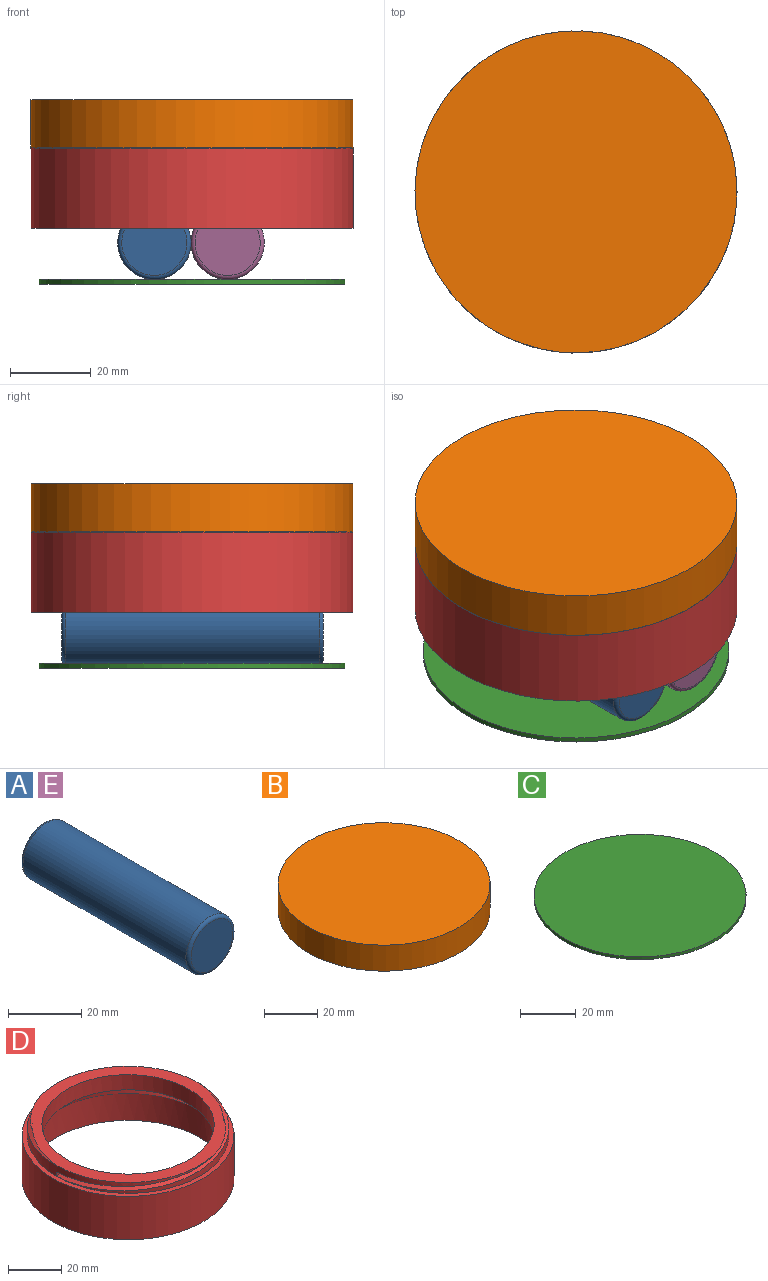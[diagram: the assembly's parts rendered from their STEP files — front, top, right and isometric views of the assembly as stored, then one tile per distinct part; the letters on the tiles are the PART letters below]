
ASSEMBLY  parts=5 mates=3
PART A: 5 faces, bbox 19.7x65x19.7 mm
  f0: cylinder r=9.1mm len=63mm, axis (0,1,0), area 3602.2mm2, adj f3,f4
  f1: plane 16.2x16.2mm, normal (0,-1,0), area 206.1mm2, adj f4
  f2: plane 16.2x16.2mm, normal (0,1,0), area 206.1mm2, adj f3
  f3: torus R=8.1mm, axis (0,-1,0), area 86.2mm2, adj f0,f2
  f4: torus R=8.1mm, axis (0,-1,0), area 86.2mm2, adj f0,f1
PART B: 14 faces, bbox 80.5x80.5x12.5 mm
  f0: cylinder r=38mm len=76mm, axis (0,0,-1), area 406mm2, adj f4,f6,f8,f10,f12
  f1: cylinder r=38mm len=76mm, axis (0,0,-1), area 406mm2, adj f4,f6,f9,f11,f13
  f2: cylinder r=40mm len=80mm, axis (0,0,-1), area 3015.9mm2, adj f3,f4
  f3: plane 80x80mm, normal (0,0,1), area 5026.5mm2, adj f2
  f4: plane 80x80mm, normal (0,0,-1), area 490.1mm2, adj f0,f1,f2
  f5: cylinder r=36mm len=72mm, axis (0,0,1), area 1131mm2, adj f6,f7
  f6: plane 76.52x76.52mm, normal (0,0,-1), area 383.5mm2, adj f0,f1,f5,f9,f10,f12,f13
  f7: plane 72x72mm, normal (0,0,-1), area 4071.5mm2, adj f5
  f8: plane 2x1.73mm, normal (0,-1,0), area 1.7mm2, adj f0,f9,f10
  f9: bspline ~76x38mm, area 210.6mm2, adj f1,f6,f8,f10
  f10: bspline ~76x38mm, area 163.6mm2, adj f0,f6,f8,f9
  f11: plane 2x1.73mm, normal (0,1,0), area 1.7mm2, adj f1,f12,f13
  f12: bspline ~76x38mm, area 210.6mm2, adj f0,f6,f11,f13
  f13: bspline ~76x38mm, area 163.6mm2, adj f1,f6,f11,f12
PART C: 3 faces, bbox 76x76x1.2 mm
  f0: cylinder r=38mm len=76mm, axis (0,0,-1), area 286.5mm2, adj f1,f2
  f1: plane 76x76mm, normal (0,0,1), area 4536.5mm2, adj f0
  f2: plane 76x76mm, normal (0,0,-1), area 4536.5mm2, adj f0
PART D: 15 faces, bbox 80.2x80.2x27.2 mm
  f0: cylinder r=32.5mm len=65mm, axis (0,0,1), area 1429.4mm2, adj f6,f14
  f1: cylinder r=38mm len=76mm, axis (0,0,1), area 406mm2, adj f5,f6,f7,f8,f12
  f2: cylinder r=38mm len=76mm, axis (0,0,1), area 406mm2, adj f5,f6,f9,f10,f11
  f3: cylinder r=40mm len=80mm, axis (0,0,-1), area 5026.5mm2, adj f4,f5
  f4: plane 80x80mm, normal (0,0,-1), area 490.1mm2, adj f3,f13
  f5: plane 80x80mm, normal (0,0,1), area 490.1mm2, adj f1,f2,f3
  f6: plane 76.17x76.17mm, normal (0,0,1), area 1136.7mm2, adj f0,f1,f2,f8,f9,f11,f12
  f7: plane 2x1.73mm, normal (0,1,0), area 1.7mm2, adj f1,f8,f9
  f8: bspline ~76x38mm, area 163.3mm2, adj f1,f6,f7,f9
  f9: bspline ~76x38mm, area 210.7mm2, adj f2,f6,f7,f8
  f10: plane 2x1.73mm, normal (0,-1,0), area 1.7mm2, adj f2,f11,f12
  f11: bspline ~76x38mm, area 163.3mm2, adj f2,f6,f10,f12
  f12: bspline ~76x38mm, area 210.7mm2, adj f1,f6,f10,f11
  f13: cylinder r=38mm len=76mm, axis (0,0,-1), area 2984.5mm2, adj f4,f14
  f14: cone r=32.5mm half-angle=45deg, axis (0,0,-1), area 1722.7mm2, adj f0,f13
PART E: same geometry as A
PLACE A t=(-8.13,23.75,-13.9)mm
PLACE B rot(axis=(0,0,1),179.5deg) t=(1.22,-8.61,9.65)mm
PLACE C rot(axis=(0,0,1),34.7deg) t=(1.22,-8.61,-24.2)mm
PLACE D t=(1.22,-8.61,-10.33)mm fixed
PLACE E t=(10.07,23.75,-13.9)mm
MATE planar E.f0 <-> A.f0  axis (0,-1,0) through (10.07,-41.25,-13.9)mm
MATE cylindrical B.f0 <-> D.f0  axis (0,0,-1) through (1.22,-8.61,9.65)mm
MATE cylindrical C.f0 <-> D.f0  axis (0,0,1) through (1.22,-8.61,-23)mm
